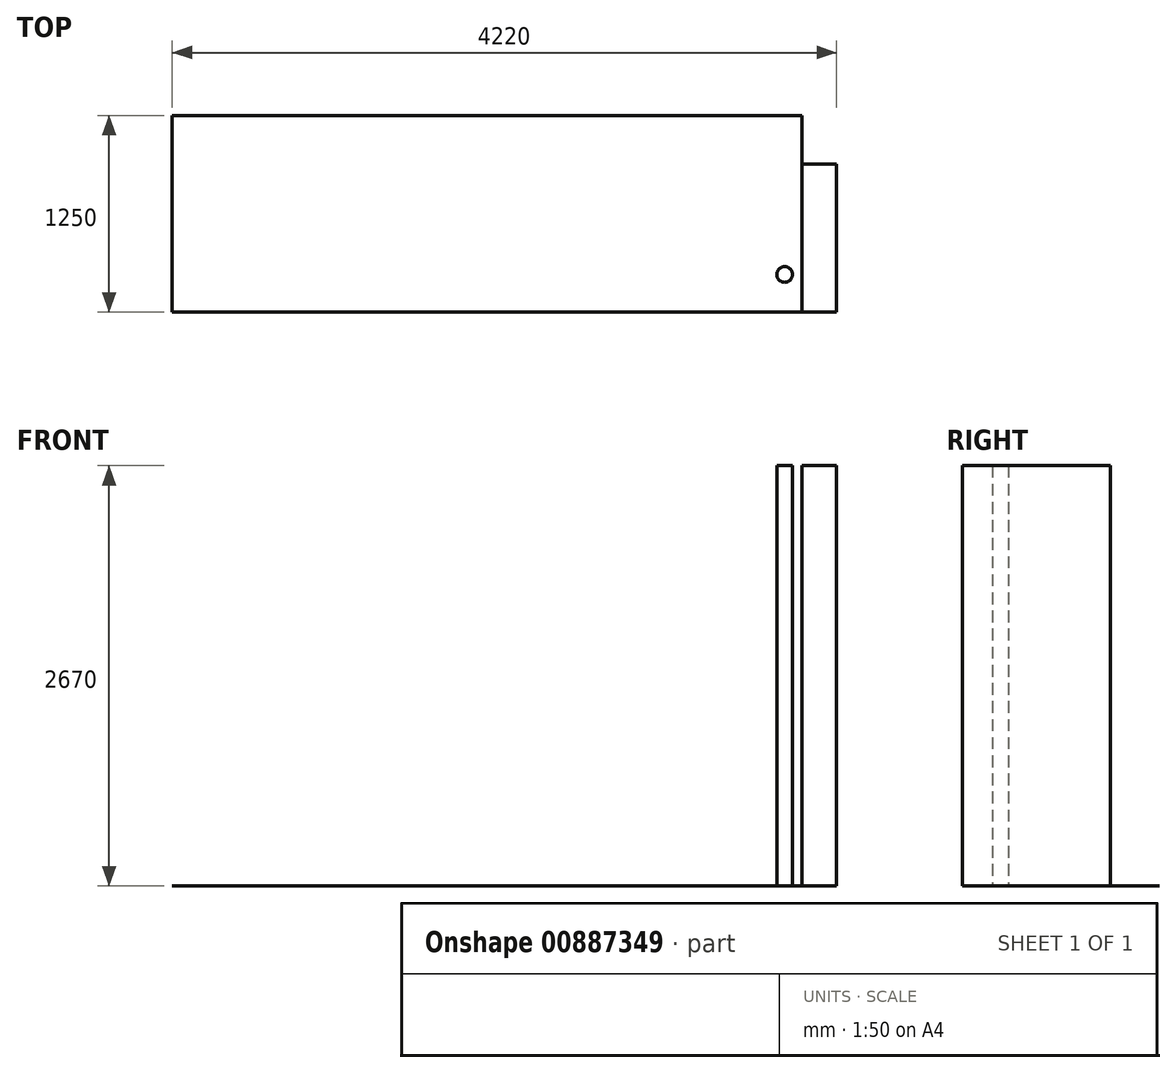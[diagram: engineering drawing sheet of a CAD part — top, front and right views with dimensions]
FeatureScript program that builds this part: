
annotation { "Feature Type Name" : "Feature", "Feature Type Description" : "" }
export const myFeature = defineFeature(function(context is Context, id is Id, definition is map)
    precondition{}
    {
        {
            var Q0;
            Q0=qCreatedBy(makeId("Top.planeOp"),FACE);
            var sketch = newSketch(context, id + "F0", { "sketchPlane" : qUnion([Q0])});
            skLineSegment(sketch, "E0.bottom", {"start": v(-4000, 0) * mm, "end": v(0, 0) * mm});
            skLineSegment(sketch, "E0.top", {"start": v(-4000, -1250) * mm, "end": v(0, -1250) * mm});
            skLineSegment(sketch, "E0.left", {"start": v(-4000, 0) * mm, "end": v(-4000, -1250) * mm});
            skLineSegment(sketch, "E0.right", {"start": v(0, 0) * mm, "end": v(0, -1250) * mm});
            skLineSegment(sketch, "E1.bottom", {"start": v(0, -310) * mm, "end": v(220, -310) * mm});
            skLineSegment(sketch, "E1.top", {"start": v(0, -1250) * mm, "end": v(220, -1250) * mm});
            skLineSegment(sketch, "E1.left", {"start": v(0, -310) * mm, "end": v(0, -1250) * mm});
            skLineSegment(sketch, "E1.right", {"start": v(220, -310) * mm, "end": v(220, -1250) * mm});
            skCircle(sketch, "E2", {"center": v(-110, -1010) * mm, "radius": 50 * mm});
            skSolve(sketch);
        }
        {
            var Q0;
            {var subQ3=sQuery(id+"F0.wireOp",EDGE,"E0.bottom");Q0=makeQuery(id+"F0.imprint","IMPRINT",FACE,{"disambiguationData":[TD([[makeQuery(id+"F0.imprint","IMPRINT",EDGE,{"derivedFrom":subQ3}),-1.0]])]});}
            extrude(context, id + "F1", {"entities" : qUnion([Q0]), "depth" : 1 * mm, "offsetDistance" : 25 * mm});
        }
        {
            var Q0;
            {var subQ2=sQuery(id+"F0.wireOp",EDGE,"E1.bottom");Q0=makeQuery(id+"F0.imprint","IMPRINT",FACE,{"disambiguationData":[TD([[makeQuery(id+"F0.imprint","IMPRINT",EDGE,{"derivedFrom":subQ2}),-1.0]])]});}
            var Q1;
            Q1=makeQuery(id+"F0.imprint","IMPRINT",FACE,{"disambiguationData":[TD([[makeQuery(id+"F0.imprint","IMPRINT",EDGE,{"derivedFrom":sQuery(id+"F0.wireOp",EDGE,"E2")}),1.0]])]});
            extrude(context, id + "F2", {"entities" : qUnion([Q0, Q1]), "operationType" : NewBodyOperationType.ADD, "depth" : 2670 * mm, "offsetDistance" : 25 * mm});
        }
    });
